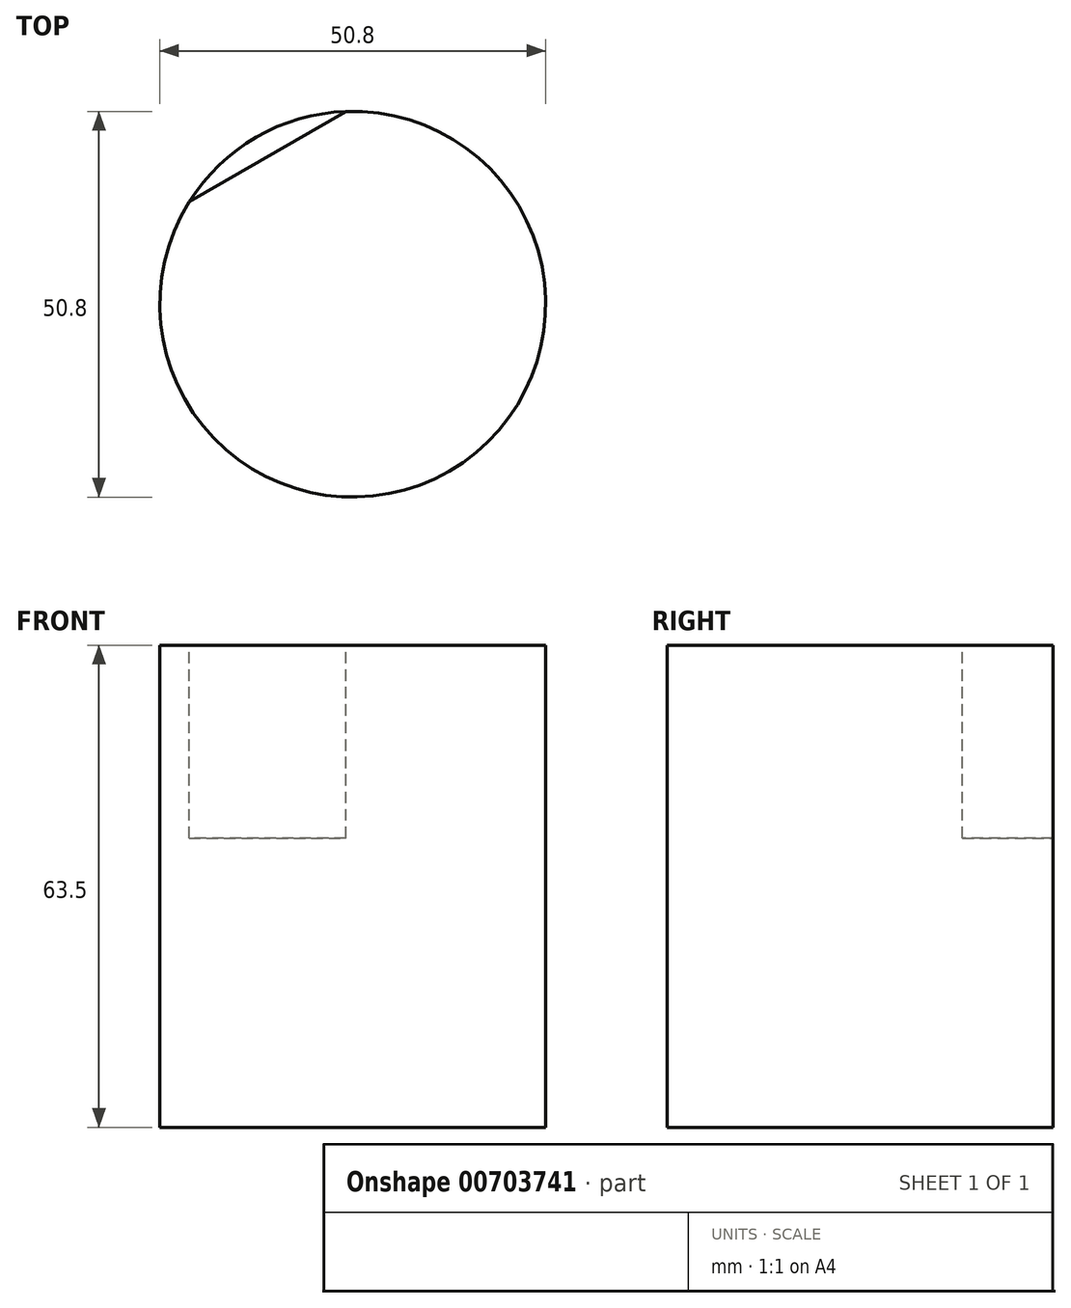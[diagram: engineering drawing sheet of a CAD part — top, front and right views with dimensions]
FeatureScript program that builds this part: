
annotation { "Feature Type Name" : "Feature", "Feature Type Description" : "" }
export const myFeature = defineFeature(function(context is Context, id is Id, definition is map)
    precondition{}
    {
        {
            var Q0;
            Q0=qCreatedBy(makeId("Top.planeOp"),FACE);
            var sketch = newSketch(context, id + "F0", { "sketchPlane" : qUnion([Q0])});
            skCircle(sketch, "E0", {"center": v(0, 0) * mm, "radius": 25.4 * mm});
            skSolve(sketch);
        }
        {
            var Q0;
            Q0=makeQuery(id+"F0.imprint","IMPRINT",FACE,{"disambiguationData":[TD([[makeQuery(id+"F0.imprint","IMPRINT",EDGE,{"derivedFrom":sQuery(id+"F0.wireOp",EDGE,"E0")}),1.0]])]});
            extrude(context, id + "F1", {"entities" : qUnion([Q0]), "depth" : 63.5 * mm, "offsetDistance" : 25.4 * mm});
        }
        {
            var Q0;
            Q0=makeQuery(id+"F1.opExtrude","CAP_FACE",FACE,{"disambiguationData":[OSD([sQuery(id+"F0.wireOp",EDGE,"E0")])],"isStart":false});
            var sketch = newSketch(context, id + "F2", { "sketchPlane" : qUnion([Q0])});
            skCircle(sketch, "E1.cCircle", {"center": v(0, 0) * mm, "radius": 22.43 * mm, "construction": true});
            skLineSegment(sketch, "E1.0", {"start": v(22.43, 12.95) * mm, "end": v(22.43, -12.95) * mm});
            skLineSegment(sketch, "E1.1", {"start": v(22.43, -12.95) * mm, "end": v(0, -25.9) * mm});
            skLineSegment(sketch, "E1.2", {"start": v(0, -25.9) * mm, "end": v(-22.43, -12.95) * mm});
            skLineSegment(sketch, "E1.3", {"start": v(-22.43, -12.95) * mm, "end": v(-22.43, 12.95) * mm});
            skLineSegment(sketch, "E1.4", {"start": v(-22.43, 12.95) * mm, "end": v(0, 25.9) * mm});
            skLineSegment(sketch, "E1.5", {"start": v(0, 25.9) * mm, "end": v(22.43, 12.95) * mm});
            skPoint(sketch, "E1.0.midPoint", {"position": v(22.43, 0) * mm});
            skSolve(sketch);
        }
        {
            var Q0;
            {var subQ0=sQuery(id+"F2.wireOp",EDGE,"E1.4");var subQ1=makeQuery(id+"F1.opExtrude","CAP_EDGE",EDGE,{"disambiguationData":[OSD([sQuery(id+"F0.wireOp",EDGE,"E0")])],"isStart":false});var subQ2=makeQuery(id+"F2.imprint","INTERSECT",VERTEX,{"disambiguationData":[OD(0.0)],"derivedFrom":[subQ1,subQ0]});Q0=makeQuery(id+"F2.imprint","IMPRINT",FACE,{"disambiguationData":[TD([[makeQuery(id+"F2.imprint","IMPRINT",EDGE,{"disambiguationData":[TD([[subQ2,-1.0]])],"derivedFrom":subQ0}),1.0]])]});}
            extrude(context, id + "F3", {"entities" : qUnion([Q0]), "operationType" : NewBodyOperationType.REMOVE, "oppositeDirection" : true, "depth" : 25.4 * mm, "offsetDistance" : 25.4 * mm});
        }
    });
